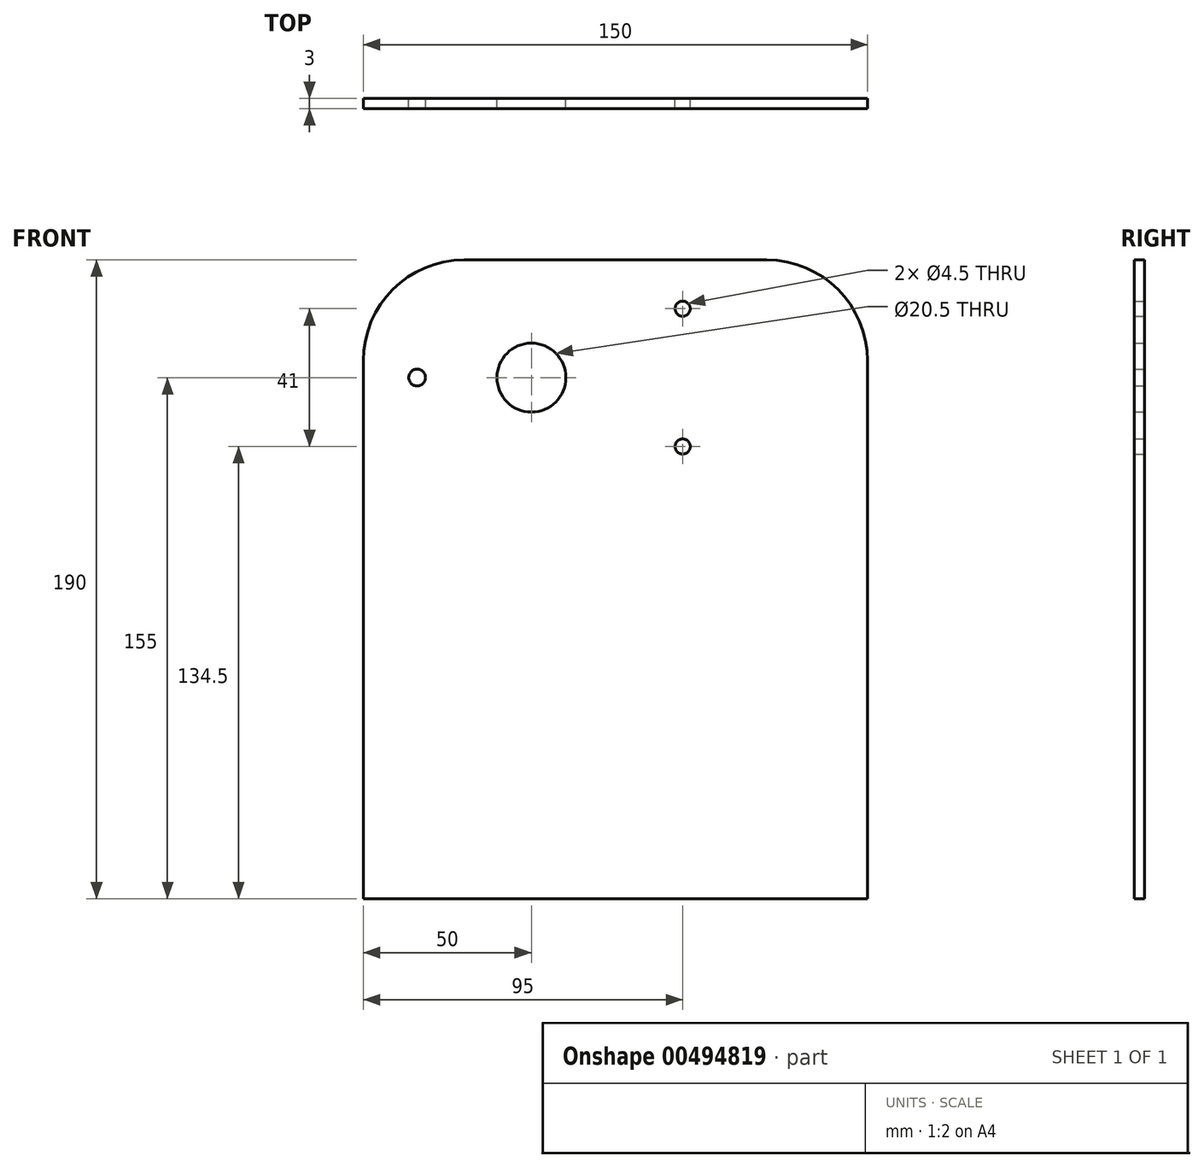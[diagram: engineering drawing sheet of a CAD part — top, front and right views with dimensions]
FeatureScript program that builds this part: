
annotation { "Feature Type Name" : "Feature", "Feature Type Description" : "" }
export const myFeature = defineFeature(function(context is Context, id is Id, definition is map)
    precondition{}
    {
        {
            var Q0;
            Q0=qCreatedBy(makeId("Front.planeOp"),FACE);
            var sketch = newSketch(context, id + "F0", { "sketchPlane" : qUnion([Q0])});
            skLineSegment(sketch, "E0.bottom", {"start": v(75, -95) * mm, "end": v(-75, -95) * mm});
            skLineSegment(sketch, "E0.top", {"start": v(75, 95) * mm, "end": v(-75, 95) * mm});
            skLineSegment(sketch, "E0.left", {"start": v(75, -95) * mm, "end": v(75, 95) * mm});
            skLineSegment(sketch, "E0.right", {"start": v(-75, -95) * mm, "end": v(-75, 95) * mm});
            skPoint(sketch, "E0.middle", {"position": v(0, 0) * mm});
            skCircle(sketch, "E1", {"center": v(-25, 60) * mm, "radius": 10.25 * mm});
            skCircle(sketch, "E2", {"center": v(-59, 60) * mm, "radius": 2.5 * mm});
            skCircle(sketch, "E3", {"center": v(20, 80.5) * mm, "radius": 2.25 * mm});
            skCircle(sketch, "E4", {"center": v(20, 39.5) * mm, "radius": 2.25 * mm});
            skPoint(sketch, "E5", {"position": v(0, 95) * mm});
            skSolve(sketch);
        }
        {
            var Q0;
            Q0 = qSketchRegion(id + "F0", true);
            extrude(context, id + "F1", {"entities" : qUnion([Q0]), "depth" : 3 * mm});
        }
        {
            var Q0;
            Q0=makeQuery(id+"F1.opExtrude","SWEPT_EDGE",EDGE,{"disambiguationData":[OSD([sQuery(id+"F0.wireOp",EDGE,"E0.top"),sQuery(id+"F0.wireOp",EDGE,"E0.left")])]});
            var Q1;
            Q1=makeQuery(id+"F1.opExtrude","SWEPT_EDGE",EDGE,{"disambiguationData":[OSD([sQuery(id+"F0.wireOp",EDGE,"E0.top"),sQuery(id+"F0.wireOp",EDGE,"E0.right")])]});
            fillet(context, id + "F2", {"entities" : qUnion([Q0, Q1]), "radius" : 30 * mm, "tangentPropagation" : true, "allowEdgeOverflow" : false});
        }
    });
